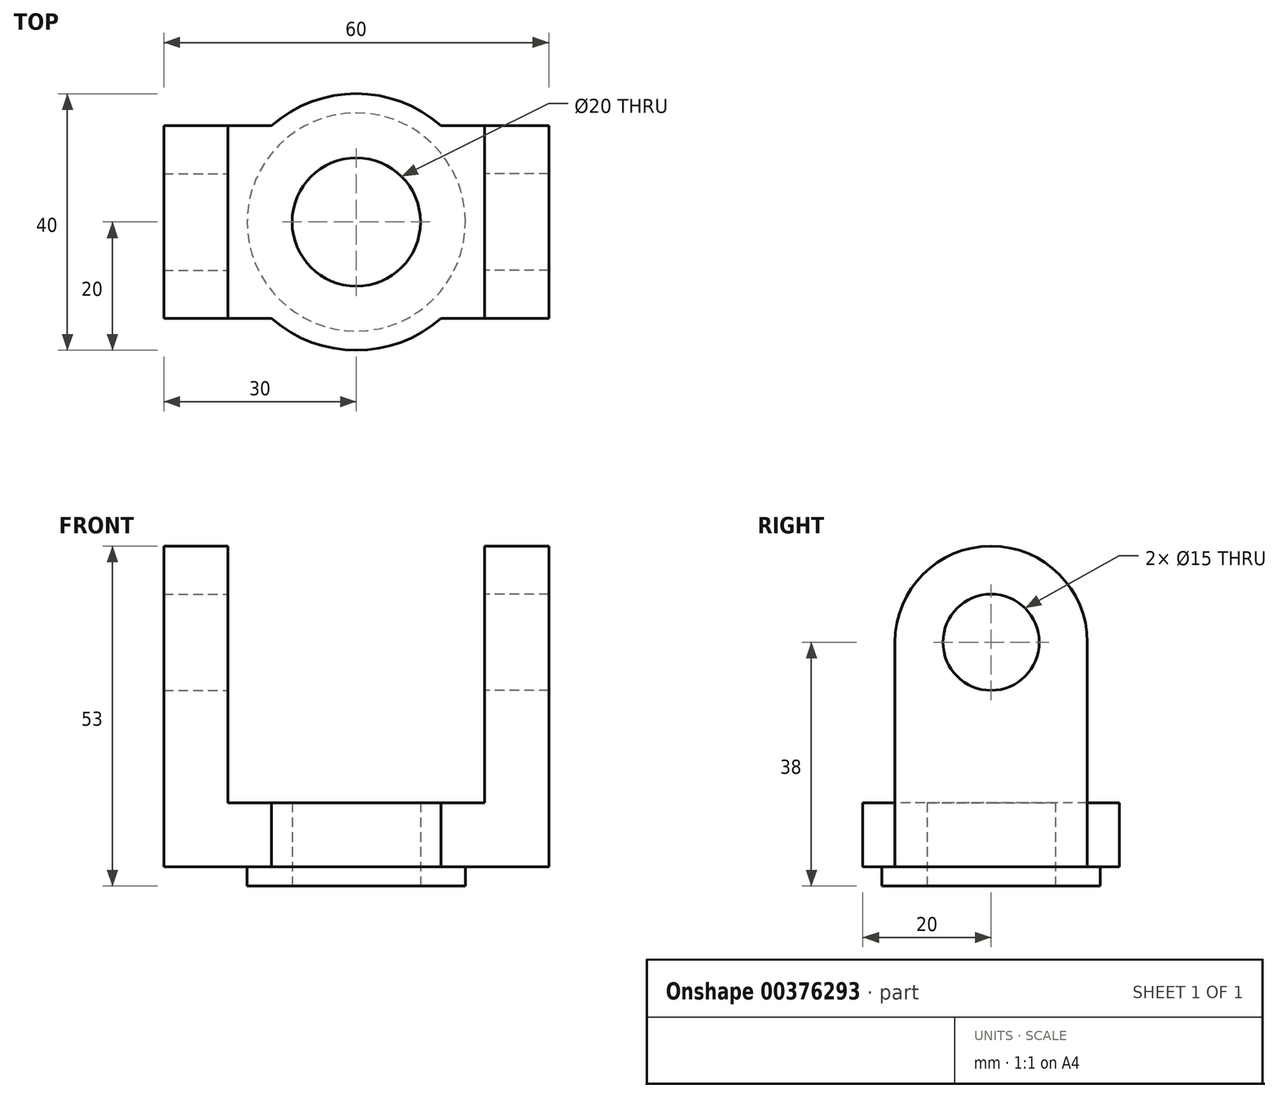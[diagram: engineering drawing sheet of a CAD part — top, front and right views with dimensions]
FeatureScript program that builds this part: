
annotation { "Feature Type Name" : "Feature", "Feature Type Description" : "" }
export const myFeature = defineFeature(function(context is Context, id is Id, definition is map)
    precondition{}
    {
        {
            var Q0;
            Q0=qCreatedBy(makeId("Top.planeOp"),FACE);
            var sketch = newSketch(context, id + "F0", { "sketchPlane" : qUnion([Q0])});
            skLineSegment(sketch, "E0.bottom", {"start": v(0, 0) * mm, "end": v(40, 0) * mm});
            skLineSegment(sketch, "E0.top", {"start": v(0, -30) * mm, "end": v(40, -30) * mm});
            skLineSegment(sketch, "E0.left", {"start": v(0, 0) * mm, "end": v(0, -30) * mm});
            skLineSegment(sketch, "E0.right", {"start": v(40, 0) * mm, "end": v(40, -30) * mm});
            skCircle(sketch, "E1", {"center": v(20, -15) * mm, "radius": 20 * mm});
            skPoint(sketch, "E1.centerSnap0", {"position": v(0, -15) * mm});
            skPoint(sketch, "E1.centerSnap1", {"position": v(20, 0) * mm});
            skCircle(sketch, "E2", {"center": v(20, -15) * mm, "radius": 10 * mm});
            skSolve(sketch);
        }
        {
            var Q0;
            {var subQ0=sQuery(id+"F0.wireOp",EDGE,"E0.left");Q0=makeQuery(id+"F0.imprint","IMPRINT",FACE,{"disambiguationData":[TD([[makeQuery(id+"F0.imprint","IMPRINT",EDGE,{"derivedFrom":subQ0}),1.0]])]});}
            var Q1;
            {var subQ0=sQuery(id+"F0.wireOp",EDGE,"E0.right");Q1=makeQuery(id+"F0.imprint","IMPRINT",FACE,{"disambiguationData":[TD([[makeQuery(id+"F0.imprint","IMPRINT",EDGE,{"derivedFrom":subQ0}),-1.0]])]});}
            var Q2;
            Q2=makeQuery(id+"F0.imprint","IMPRINT",FACE,{"disambiguationData":[TD([[makeQuery(id+"F0.imprint","IMPRINT",EDGE,{"derivedFrom":sQuery(id+"F0.wireOp",EDGE,"E2")}),-1.0]])]});
            var Q3;
            {var subQ0=sQuery(id+"F0.wireOp",EDGE,"E1");var subQ1=sQuery(id+"F0.wireOp",EDGE,"E0.bottom");var subQ2=makeQuery(id+"F0.imprint","INTERSECT",VERTEX,{"disambiguationData":[OD(0.0)],"derivedFrom":[subQ1,subQ0]});Q3=makeQuery(id+"F0.imprint","IMPRINT",FACE,{"disambiguationData":[TD([[makeQuery(id+"F0.imprint","IMPRINT",EDGE,{"disambiguationData":[TD([[subQ2,-1.0]])],"derivedFrom":subQ1}),1.0]])]});}
            var Q4;
            {var subQ0=sQuery(id+"F0.wireOp",EDGE,"E1");var subQ1=sQuery(id+"F0.wireOp",EDGE,"E0.top");var subQ2=makeQuery(id+"F0.imprint","INTERSECT",VERTEX,{"disambiguationData":[OD(0.0)],"derivedFrom":[subQ1,subQ0]});Q4=makeQuery(id+"F0.imprint","IMPRINT",FACE,{"disambiguationData":[TD([[makeQuery(id+"F0.imprint","IMPRINT",EDGE,{"disambiguationData":[TD([[subQ2,-1.0]])],"derivedFrom":subQ1}),-1.0]])]});}
            extrude(context, id + "F1", {"entities" : qUnion([Q0, Q1, Q2, Q3, Q4]), "depth" : 10 * mm});
        }
        {
            var Q0;
            Q0=makeQuery(id+"F1.opExtrude","CAP_FACE",FACE,{"disambiguationData":[OSD([sQuery(id+"F0.wireOp",EDGE,"E0.bottom"),sQuery(id+"F0.wireOp",EDGE,"E0.top"),sQuery(id+"F0.wireOp",EDGE,"E0.left"),sQuery(id+"F0.wireOp",EDGE,"E0.right"),sQuery(id+"F0.wireOp",EDGE,"E1"),sQuery(id+"F0.wireOp",EDGE,"E2")])],"isStart":true});
            var sketch = newSketch(context, id + "F2", { "sketchPlane" : qUnion([Q0])});
            skCircle(sketch, "E3", {"center": v(20, 15) * mm, "radius": 10 * mm});
            skCircle(sketch, "E4", {"center": v(20, 15) * mm, "radius": 17 * mm});
            skSolve(sketch);
        }
        {
            var Q0;
            Q0 = qSketchRegion(id + "F2", true);
            extrude(context, id + "F3", {"entities" : qUnion([Q0]), "operationType" : NewBodyOperationType.ADD, "depth" : 3 * mm});
        }
        {
            var Q0;
            Q0=makeQuery(id+"F1.opExtrude","SWEPT_FACE",FACE,{"disambiguationData":[OSD([sQuery(id+"F0.wireOp",EDGE,"E0.right")])]});
            var sketch = newSketch(context, id + "F4", { "sketchPlane" : qUnion([Q0])});
            skLineSegment(sketch, "E5", {"start": v(-30, 0) * mm, "end": v(-30, 35) * mm});
            skPoint(sketch, "E5.endSnap0", {"position": v(-30, 5) * mm});
            skLineSegment(sketch, "E6", {"start": v(-30, 0) * mm, "end": v(0, 0) * mm});
            skLineSegment(sketch, "E7", {"start": v(0, 0) * mm, "end": v(0, 35) * mm});
            skPoint(sketch, "E7.endSnap0", {"position": v(0, 5) * mm});
            skArc(sketch, "E8", {"start": v(0, 35) * mm, "mid": v(-15, 50) * mm, "end": v(-30, 35) * mm});
            skCircle(sketch, "E9", {"center": v(-15, 35) * mm, "radius": 7.5 * mm});
            skSolve(sketch);
        }
        {
            var Q0;
            Q0 = qSketchRegion(id + "F4", true);
            extrude(context, id + "F5", {"entities" : qUnion([Q0]), "operationType" : NewBodyOperationType.ADD, "depth" : 10 * mm});
        }
        {
            var Q0;
            Q0=makeQuery(id+"F1.opExtrude","SWEPT_FACE",FACE,{"disambiguationData":[OSD([sQuery(id+"F0.wireOp",EDGE,"E0.left")])]});
            var sketch = newSketch(context, id + "F6", { "sketchPlane" : qUnion([Q0])});
            skLineSegment(sketch, "E10", {"start": v(0, 35) * mm, "end": v(0, 0) * mm});
            skLineSegment(sketch, "E11", {"start": v(0, 0) * mm, "end": v(30, 0) * mm});
            skLineSegment(sketch, "E12", {"start": v(30, 0) * mm, "end": v(30, 35) * mm});
            skPoint(sketch, "E12.endSnap0", {"position": v(30, 5) * mm});
            skArc(sketch, "E13", {"start": v(30, 35) * mm, "mid": v(15, 50) * mm, "end": v(0, 35) * mm});
            skCircle(sketch, "E14", {"center": v(15, 35) * mm, "radius": 7.5 * mm});
            skSolve(sketch);
        }
        {
            var Q0;
            Q0 = qSketchRegion(id + "F6", true);
            extrude(context, id + "F7", {"entities" : qUnion([Q0]), "operationType" : NewBodyOperationType.ADD, "depth" : 10 * mm});
        }
    });
